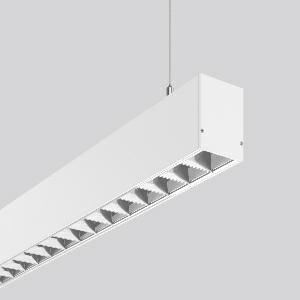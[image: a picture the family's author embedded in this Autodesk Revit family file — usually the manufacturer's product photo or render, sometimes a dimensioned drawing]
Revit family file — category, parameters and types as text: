
# Revit family: less_is_more_50_312336_002_76_e9b7
name_source: partatom
category: Lighting Fixtures
units: mm (PartAtom-declared; Revit-internal decimal feet)

## family parameters
Cut with Voids When Loaded = No
Host = Face
Light Source = No
Part Type = Normal
Room Calculation Point = No
Round Connector Dimension = Use Diameter
Shared = No

## types (1)
- LESS IS MORE 50 (1 x LED Modul 830, 3350 lm, 3000)
    Apparent Load = 28 VA
    CIE Flux Codes = 95 100 100 100 100
    Color Rendering = 80
    Color Temperature = 3000
    Default Elevation = 1800 mm
    Description = Series: LESS IS MORE 50
Linear pendant luminaire for aesthetically sophisticated lighting. Housing: extruded aluminium profile, powder-coated. End cap aluminium powder-coated. Canopy made of aluminium, powder-coated. Alea optical system: Reflector structure (ABS, Aluminium-coated, highly polished) with integrated diffuser made of non-yellowing plastic (PMMA) opal for glare-free light at the workstation (screen-compliant according to EN 12464-1). Direct light emission. Suitable for pendant. 2-point steel cable suspension freely positionable and infinitely height-adjustable. Special lengths available on request. LED unit with integrated converter interchangeable and removable. Suitable for through-wiring. With sensors or as a safety luminaire on request. 
Colour: traffic white, matt (RAL 9016)
Length: 1127 mm
Width: 57 mm
Height: 75 mm
Suspension length: 2000 mm
Lamp: LED
Socket: without socket
Colour temperature: 3000K
Colour rendering index (CRI): 80
System power: 28 W
Rated luminous flux: 3350 lm
Luminous efficiency: 120 lm/W
Control gear: Converter, dimmable, DALI
Protection class: I
Type of protection: IP 20
    Height = 75 mm
    Lamp = 1 x LED Modul 830
    Lamp Light Flux = 3350 lm
    Lamp count = 1
    Length = 1127 mm
    Lifetime = 50000 h
    Luminous efficacy = 120 lm/W
    Manufacturer = RZB
    ModVariant = No
    Model = 312336.002.76
    Mounting Place = Ceiling
    Mounting Type = Pendant
    Number of Poles = 1
    OnlyDefault = Yes
    Power Factor = 1
    Product Name = LESS IS MORE 50
    Product group = Pendant LED linear luminaires
    ProductGroupID = 907
    Protection Class = Protection class I
    Protection Degree = IP 20
    RLX_Detail_Level = 1
    RLX_Emergency_Light_Flux = 0 lm
    RLX_Emergency_Type = 0
    RLX_Emergency_Type_DB = No
    RlxData = <blob elided: 33201 chars, md5=875076cd>
    Socket = socket
    Standby Power = 0 W
    System Light Flux = 3350 lm
    System Power = 28 W
    Type Comments = Product without accessories
    Type Image = 312342.002.jpg
    URL = http://relux.com
    VarID = ---
    Voltage = 230 V
    Voltage Range = 220-240 V
    Weight = 0.00 kg
    Width = 57 mm

## geometry (parser evidence)
native form markers: Blend x4, Sweep x9
no freeform markers — native parametric forms only
